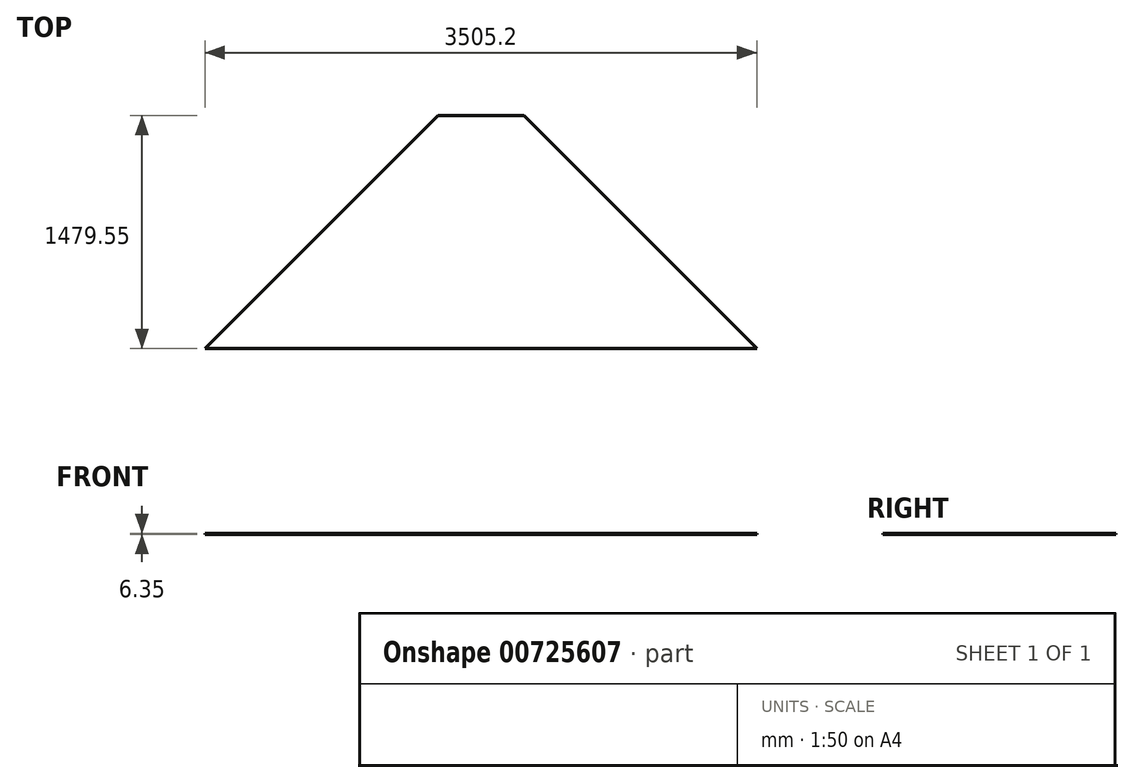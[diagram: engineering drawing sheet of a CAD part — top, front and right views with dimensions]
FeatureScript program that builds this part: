
annotation { "Feature Type Name" : "Feature", "Feature Type Description" : "" }
export const myFeature = defineFeature(function(context is Context, id is Id, definition is map)
    precondition{}
    {
        {
            var Q0;
            Q0=qCreatedBy(makeId("Top.planeOp"),FACE);
            var sketch = newSketch(context, id + "F0", { "sketchPlane" : qUnion([Q0])});
            skLineSegment(sketch, "E0", {"start": v(-1752.6, 0) * mm, "end": v(1752.6, 0) * mm});
            skLineSegment(sketch, "E1", {"start": v(1752.6, 0) * mm, "end": v(273.05, 1479.55) * mm});
            skLineSegment(sketch, "E2", {"start": v(273.05, 1479.55) * mm, "end": v(-273.05, 1479.55) * mm});
            skLineSegment(sketch, "E3", {"start": v(-273.05, 1479.55) * mm, "end": v(-1752.6, 0) * mm});
            skSolve(sketch);
        }
        {
            var Q0;
            Q0 = qSketchRegion(id + "F0", true);
            extrude(context, id + "F1", {"entities" : qUnion([Q0]), "depth" : 6.35 * mm, "offsetDistance" : 25.4 * mm});
        }
    });
